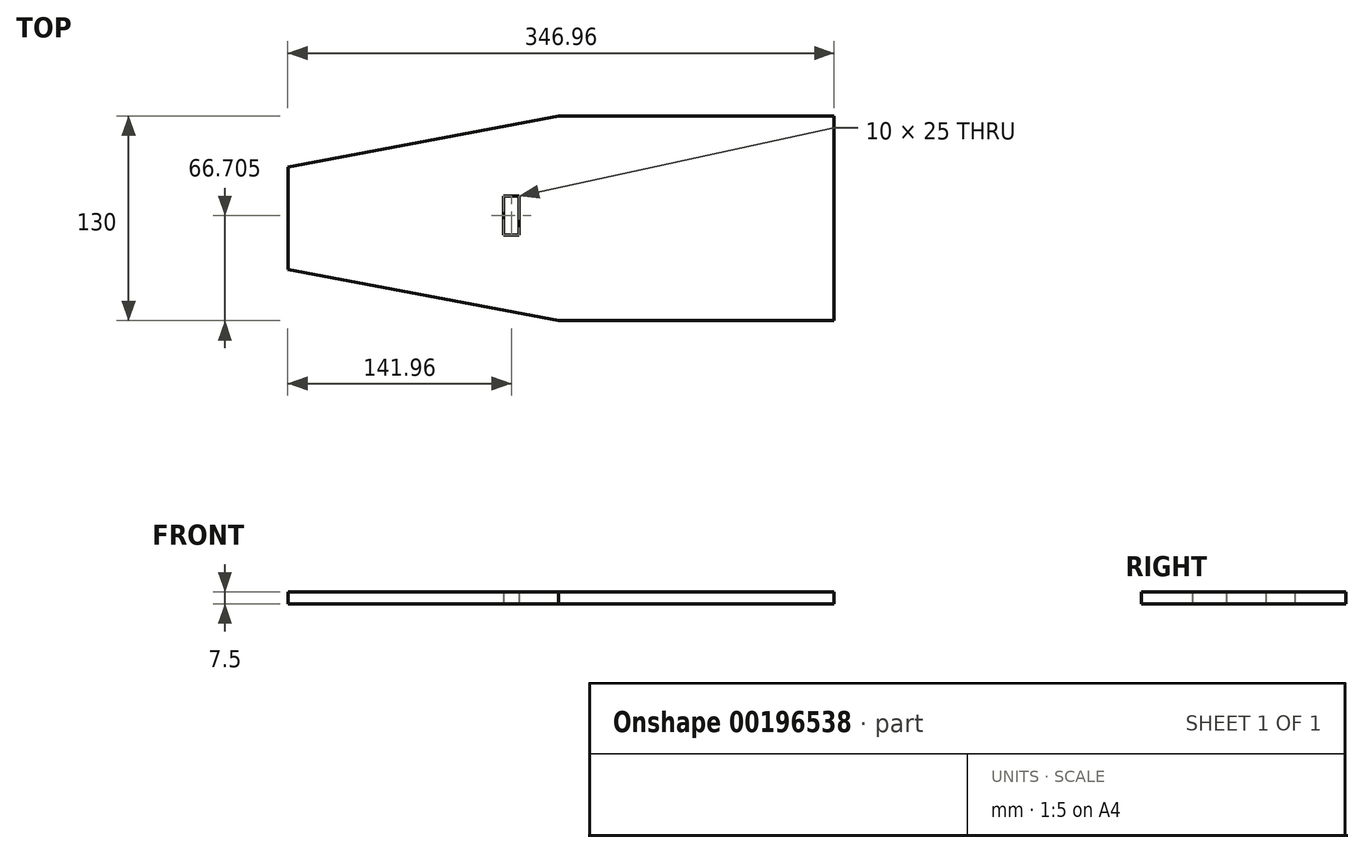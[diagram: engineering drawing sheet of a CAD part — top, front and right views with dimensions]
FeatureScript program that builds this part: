
annotation { "Feature Type Name" : "Feature", "Feature Type Description" : "" }
export const myFeature = defineFeature(function(context is Context, id is Id, definition is map)
    precondition{}
    {
        {
            var Q0;
            Q0=qCreatedBy(makeId("Top.planeOp"),FACE);
            var sketch = newSketch(context, id + "F0", { "sketchPlane" : qUnion([Q0])});
            skLineSegment(sketch, "E0.bottom", {"start": v(0, 65) * mm, "end": v(175, 65) * mm});
            skLineSegment(sketch, "E0.top", {"start": v(0, -65) * mm, "end": v(175, -65) * mm});
            skLineSegment(sketch, "E0.left", {"start": v(0, 65) * mm, "end": v(0, -65) * mm});
            skLineSegment(sketch, "E0.right", {"start": v(175, 65) * mm, "end": v(175, -65) * mm});
            skLineSegment(sketch, "E1", {"start": v(-171.96, 32.5) * mm, "end": v(-171.96, -32.5) * mm});
            skLineSegment(sketch, "E2", {"start": v(-171.96, 32.5) * mm, "end": v(0, 65) * mm});
            skLineSegment(sketch, "E3", {"start": v(-171.96, -32.5) * mm, "end": v(0, -65) * mm});
            skSolve(sketch);
        }
        {
            var Q0;
            Q0 = qSketchRegion(id + "F0", true);
            extrude(context, id + "F1", {"entities" : qUnion([Q0]), "depth" : 7.5 * mm});
        }
        {
            var Q0;
            Q0=qCreatedBy(makeId("Top.planeOp"),FACE);
            var sketch = newSketch(context, id + "F2", { "sketchPlane" : qUnion([Q0])});
            skLineSegment(sketch, "E4.bottom", {"start": v(-35, 14.2) * mm, "end": v(-25, 14.2) * mm});
            skLineSegment(sketch, "E4.top", {"start": v(-35, -10.8) * mm, "end": v(-25, -10.8) * mm});
            skLineSegment(sketch, "E4.left", {"start": v(-35, 14.2) * mm, "end": v(-35, -10.8) * mm});
            skLineSegment(sketch, "E4.right", {"start": v(-25, 14.2) * mm, "end": v(-25, -10.8) * mm});
            skSolve(sketch);
        }
        {
            var Q0;
            Q0 = qSketchRegion(id + "F2", true);
            extrude(context, id + "F3", {"entities" : qUnion([Q0]), "operationType" : NewBodyOperationType.REMOVE, "depth" : 7.5 * mm});
        }
    });
